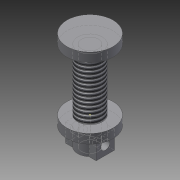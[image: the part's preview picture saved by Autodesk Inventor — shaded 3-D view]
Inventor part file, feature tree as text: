
AUTODESK INVENTOR PART (.ipt)
format: ipt  version: 2015 (Build 190159000, 159)  size: 160,768 bytes
history: native  units: mm
features: sketch x11, extrude x7, hole x2, thread x1
ambient origin geometry x8: Origin, YZ Plane, XZ Plane, XY Plane, X Axis, Y Axis, Z Axis, Center Point
bodies: Solid1 (feature_tree)
feature tree (21):
  extrude  "Extrusion1"  Depth=5.5mm
  extrude  "Extrusion2"  Depth=20.0mm
  sketch  "Sketch3"  dims[d5=3.0mm d6=0.0mm d7=5.5mm]
  extrude  "Extrusion3"  Depth=5.5mm
  extrude  "Extrusion4"  Depth=3.0mm TaperAngle=0.0deg
  extrude  "Extrusion5"  Depth=3.0mm
  extrude  "Extrusion6"  Depth=6.0mm TaperAngle=0.0deg
  extrude  "Extrusion7"  Depth=20.0mm TaperAngle=0.0deg
  hole  "Hole1"  [1 undecoded]
  hole  "Hole2"  [1 undecoded]
  sketch  "3D Sketch1"
  thread  "Thread1"  [1 undecoded]
  sketch  "Sketch1"  dims[d0=5.5mm d1=8.0mm]
  sketch  "Sketch2"  dims[d2=20.0mm d3=0.0mm d4=15.0mm]
  sketch  "Sketch4"  dims[d8=15.0mm d9=3.0mm d10=0.0mm]
  sketch  "Sketch5"  dims[d11=6.0mm d12=0.0mm d13=3.0mm]
  sketch  "Sketch6"  dims[d14=3.0mm d15=6.0mm d16=0.0mm]
  sketch  "Sketch7"  dims[d17=3.0mm d18=20.0mm d19=0.0mm]
  sketch  "Sketch8"  dims[d20=3.0mm d21=3.0mm]
  sketch  "Sketch9"  dims[d22=5.0mm d23=2.75mm d24=2.75mm]
  sketch  "Sketch10"  dims[d25=5.0mm d26=6.0mm d27=0.0mm d28=3.0mm d29=6.0mm d30=5.0mm d31=2.0mm d32=90.0deg d33=8.0mm d34=20.594885mm d35=3.0mm d36=6.0mm d37=5.0mm d38=2.0mm d39=90.0deg d40=8.0mm d41=20.594885mm d42=10.0mm d43=0.0mm]
note: 3 required parameter values undecoded (feature->parameter linkage not recoverable at this tier; creation-order binding heuristic only, values carry confidence <= 0.55)
